# Revit family: Furniture_Chairs-Stools-Benches_Bla-Station_Stove
name_source: partatom
category: Furniture
units: mm (PartAtom-declared; Revit-internal decimal feet)

## family parameters
Always vertical = Yes
Cut with Voids When Loaded = No
OmniClass Number = 23.40.20.14.14.11
OmniClass Title = Chairs
Room Calculation Point = No
Shared = No
Work Plane-Based = No

## types (1)
- Furniture_Chairs-Stools-Benches_Bla-Station_Stove
    AssetType = Movable
    BIMObjectName = CONV_BlaStation_DmstcChrs_Stove
    Brand = Blå Station
    Category = Stools
    Collection = Stove
    Color = Various
    ConvergoRefNr = 0099-1806-0005-SE
    Cost = 0 $
    Default Elevation = 0 mm  [stored 0 ft]
    Description = Not only are our homes getting smaller today, so are restaurants, bars and cafes too. “What is the smallest functional chair, that could still be comfortable to sit on?” designer Gabriel Tan asked himself and looked into how the shaker movement designed for their way of life, Stove is a three-legged chair with a short backrest and a seat shape inspired by the shaker stove. Stove can be hung on the included wall-mounted peg, or on a peg rail.
    Design = Gabriel Tan
    DurationUnit = Year
    Edition number = 1
    Features = Wall-mounted peg included, peg rail available
    HighestSeatingHeight = 440 mm  [stored 1.44357 ft]
    IfcExportAs = IfcFurnishingElementType
    IfcExportType = CHAIR
    LowestSeatingHeight = 440 mm  [stored 1.44357 ft]
    MainColor = Wooden
    Manufacturer = Blå Station
    ManufacturerName = Blå Station
    ManufacturerURL = http://www.blastation.com
    Material = Wood
    Model = Stove
    Name = DmstcChrs_Stove
    NominalDepth = 380 mm  [stored 1.24672 ft]
    NominalHeight = 630 mm  [stored 2.06693 ft]
    NominalWidth = 335 mm  [stored 1.09908 ft]
    Product Guid = 0b956ab7-1967-4655-aed8-a6a29ad57906
    Product data url = https://www.bimobject.com
    ProductInformation = Not only are our homes getting smaller today, so are restaurants, bars and cafes too. “What is the smallest functional chair, that could still be comfortable to sit on?” designer Gabriel Tan asked himself and looked into how the shaker movement designed for their way of life, Stove is a three-legged chair with a short backrest and a seat shape inspired by the shaker stove. Stove can be hung on the included wall-mounted peg, or on a peg rail.
    SeatingHeight = 440 mm  [stored 1.44357 ft]
    Shape = Sculptured
    Size = 335x380x630 mm
    URL = http://www.blastation.com
    Uniclass2 = Pr_40_50_12_83
    Uniclass2015Description = Stools
    Uniclass2015Reference = Pr_40_50_12_85
    Version = 1
    VersionDate = 16/01/2019
    WarrantyDurationUnit = Year
    Weight = 4.1 kg

note: [stored X ft] marks values corroborated as IEEE doubles in the binary element streams (Revit-internal decimal feet)

## geometry (parser evidence)
native form markers: Sweep x2
no freeform markers — native parametric forms only
